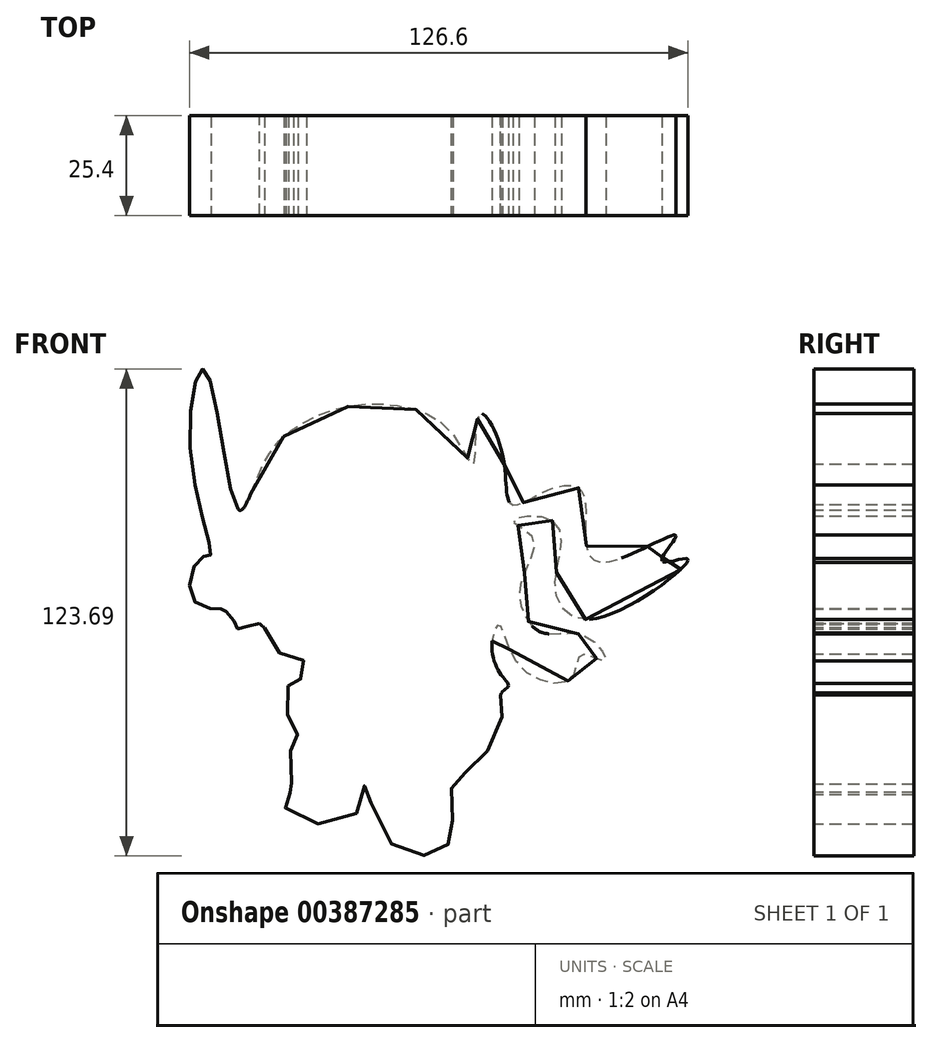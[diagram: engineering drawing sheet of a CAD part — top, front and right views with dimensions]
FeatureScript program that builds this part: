
annotation { "Feature Type Name" : "Feature", "Feature Type Description" : "" }
export const myFeature = defineFeature(function(context is Context, id is Id, definition is map)
    precondition{}
    {
        {
            var Q0;
            Q0=qCreatedBy(makeId("Front.planeOp"),FACE);
            var sketch = newSketch(context, id + "F0", { "sketchPlane" : qUnion([Q0])});
            skFitSpline(sketch, "E0", {"points": [v(-48.45, 29.21) * mm, v(-41.4, 30.68) * mm, v(-31.12, 24.22) * mm, v(-22.02, 21.58) * mm, v(-9.1, 29.5) * mm, v(0, 30.68) * mm, v(8.8, 25.7) * mm], "startDerivative": vector(49.22, 21.84) * mm, "endDerivative": vector(52.86, -37.66) * mm});
            skFitSpline(sketch, "E1", {"points": [v(-48.45, 29.21) * mm, v(-41.7, 42.13) * mm, v(-27.3, 50.65) * mm, v(-11.74, 51.82) * mm, v(2.64, 44.78) * mm, v(8.22, 36.85) * mm, v(9.69, 49.47) * mm, v(15.56, 39.2) * mm, v(17.91, 26.57) * mm, v(27.01, 30.22) * mm, v(35.53, 30.22) * mm, v(36.7, 18.06) * mm, v(41.4, 11.9) * mm, v(59.6, 18.64) * mm, v(56.08, 12.19) * mm, v(62.54, 12.77) * mm, v(38.76, -2.5) * mm, v(29.07, 4.26) * mm, v(30.54, 16.88) * mm, v(27.01, 23.05) * mm, v(18.2, 22.46) * mm, v(23.2, 18.35) * mm, v(20.55, 7.78) * mm, v(20.55, 0) * mm, v(25.84, -6.02) * mm, v(36.7, -6.9) * mm, v(41.7, -13.07) * mm, v(35.53, -11.6) * mm, v(33.18, -17.47) * mm, v(20.26, -14.83) * mm, v(14.68, -3.96) * mm, v(12.92, -8.07) * mm, v(14.97, -16.3) * mm, v(17.03, -19.53) * mm, v(15.27, -21.29) * mm, v(15.56, -26.57) * mm, v(7.93, -40.37) * mm, v(2.94, -44.19) * mm, v(2.94, -55.93) * mm, v(0, -61.22) * mm, v(-12.33, -60.04) * mm, v(-19.38, -44.48) * mm, v(-22.02, -52.41) * mm, v(-39.34, -50.94) * mm, v(-38.76, -46.54) * mm, v(-37.58, -47.13) * mm, v(-38.76, -37.73) * mm, v(-36.4, -32.44) * mm, v(-38.46, -28.92) * mm, v(-38.76, -19.23) * mm, v(-36.7, -18.64) * mm, v(-34.35, -13.65) * mm, v(-40.81, -11.3) * mm, v(-46.17, -3.67) * mm, v(-51.38, -5.14) * mm, v(-52.56, -3.08) * mm, v(-55.5, 0) * mm, v(-56.08, 0) * mm, v(-63.13, 2.5) * mm, v(-61.07, 13.07) * mm, v(-58.72, 13.65) * mm, v(-63.71, 39.5) * mm, v(-59.9, 60.63) * mm, v(-51.68, 25.4) * mm, v(-48.45, 29.21) * mm]});
            skFitSpline(sketch, "E2", {"points": [v(-51.68, 25.4) * mm, v(-51.68, 18.35) * mm, v(-43.75, 7.2) * mm, v(-26.13, 10.42) * mm, v(-11.45, 6.02) * mm, v(6.75, 12.19) * mm, v(8.8, 25.7) * mm], "startDerivative": vector(-8.05, -52.42) * mm, "endDerivative": vector(-8.52, 89.88) * mm});
            skFitSpline(sketch, "E3", {"points": [v(-58.43, 13.65) * mm, v(-56.37, 6.6) * mm, v(-51.68, 6.9) * mm, v(-37.29, -4.26) * mm, v(-17.03, -5.73) * mm, v(-6.46, 0) * mm, v(4.11, 3.96) * mm, v(6.75, 12.19) * mm], "startDerivative": vector(9.2, -83.44) * mm, "endDerivative": vector(7.1, 76.11) * mm});
            skFitSpline(sketch, "E4", {"points": [v(-52.56, 6.6) * mm, v(-46.17, -3.67) * mm, v(-25.84, -10.13) * mm, v(0, -3.67) * mm, v(6.46, 0) * mm, v(9.27, 20.79) * mm], "startDerivative": vector(27.22, -64.69) * mm, "endDerivative": vector(4.2, 115.34) * mm});
            skFitSpline(sketch, "E5", {"points": [v(10.86, 41.84) * mm, v(13.21, 27.16) * mm, v(10.86, 0) * mm, v(5.58, -14.83) * mm], "startDerivative": vector(10.39, -44.2) * mm, "endDerivative": vector(-19.15, -43.03) * mm});
            skFitSpline(sketch, "E6", {"points": [v(6.46, 0) * mm, v(3.23, -10.13) * mm, v(-6.46, -14.83) * mm, v(2.94, -23.05) * mm, v(15.27, -21.29) * mm, v(10.86, -14.83) * mm, v(12.92, -8.07) * mm], "startDerivative": vector(-2.42, -69.7) * mm, "endDerivative": vector(32.08, 48.46) * mm});
            skSolve(sketch);
        }
        {
            var Q0;
            Q0 = qSketchRegion(id + "F0", true);
            extrude(context, id + "F1", {"entities" : qUnion([Q0]), "depth" : 25.4 * mm});
        }
    });
